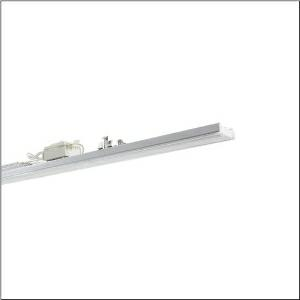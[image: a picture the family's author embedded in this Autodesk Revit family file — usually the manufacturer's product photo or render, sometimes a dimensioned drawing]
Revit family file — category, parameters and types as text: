
# Revit family: licross_r__11_recessed_mo_51te1emn495g_ba6e
name_source: partatom
category: Lighting Fixtures
units: mm (PartAtom-declared; Revit-internal decimal feet)

## family parameters
Cut with Voids When Loaded = No
Host = Face
Light Source = No
Part Type = Normal
Room Calculation Point = No
Round Connector Dimension = Use Diameter
Shared = No

## types (1)
- --- (1 x LED, 9950 lm, 55.2 W, 4000K)
    Apparent Load = 55 VA
    CIE Flux Codes = 85 95 99 100 100
    Color Rendering = 80
    Color Temperature = 4000K
    Default Elevation = 1800 mm
    Description = Licross® 11 Recessed MO, luminaire insert, of sheet steel, galvanised, coil coated, white, length: 1.500mm, width: 66mm, height: 67mm, LED rated luminous flux: 9.950lm, light colour: 840, control gear: ON/OFF Multilumen, with plug, 3-pole, with phase selection, mains connection: 220..240V, AC, 50/60Hz, rated input power: 55W, internal wiring halogen-free, primary light control with lens, of plastic, primary optical cover: cover, of PMMA, light emission: direct distribution, primary light characteristic: symmetric, protection rating (complete): IP54, insulation class (complete): insulation class I (protective earthing), certification: CE, ENEC, VDE, UKCA, protection symbol: D if used in an environment with non-conductive dust loads with corresponding accessories, impact resistance: IK06, permissible ambient temperature for indoor applications: -35..+40°C, corresponds to IFS (International Featured Standards) requirements for safety and quality in the food industry, reducing of maximum allowable ambient temperature of 5°C with ceiling mounting, packaging unit: 1 piece
    Height = 58 mm
    Lamp = 1 x LED
    Lamp Light Flux = 9950 lm
    Lamp Power = 55.2 W
    Lamp count = 1
    Length = 1500 mm
    Luminous efficacy = 180 lm/W
    Manufacturer = Siteco
    ModVariant = No
    Model = 51TE1EMN495G
    Mounting Place = Ceiling
    Mounting Type = Pendant
    Number of Poles = 1
    OnlyDefault = Yes
    Power Factor = 1
    Product Name = Licross® 11 Recessed MO
    Product group = luminaire insert | ceiling pendant
    ProductGroupID = 902
    Protection Class = Protection class I
    Protection Degree = IP 54
    RLX_Detail_Level = 1
    RLX_Emergency_Light_Flux = 0 lm
    RLX_Emergency_Type = 0
    RLX_Emergency_Type_DB = No
    RlxData = <blob elided: 22293 chars, md5=8e09d7d0>
    Socket = socket
    Standby Power = 0 W
    System Light Flux = 9950 lm
    System Power = 55 W
    Type Comments = factory setting: luminous flux: 100 % | (A | C | E) | 126 mA
    Type Image = l_1296930.jpg
    URL = http://relux.com
    VarID = @adj_105793
    Voltage = 0 V
    Weight = 0.00 kg
    Width = 66 mm

## geometry (parser evidence)
native form markers: Blend x4, Sweep x12
no freeform markers — native parametric forms only
